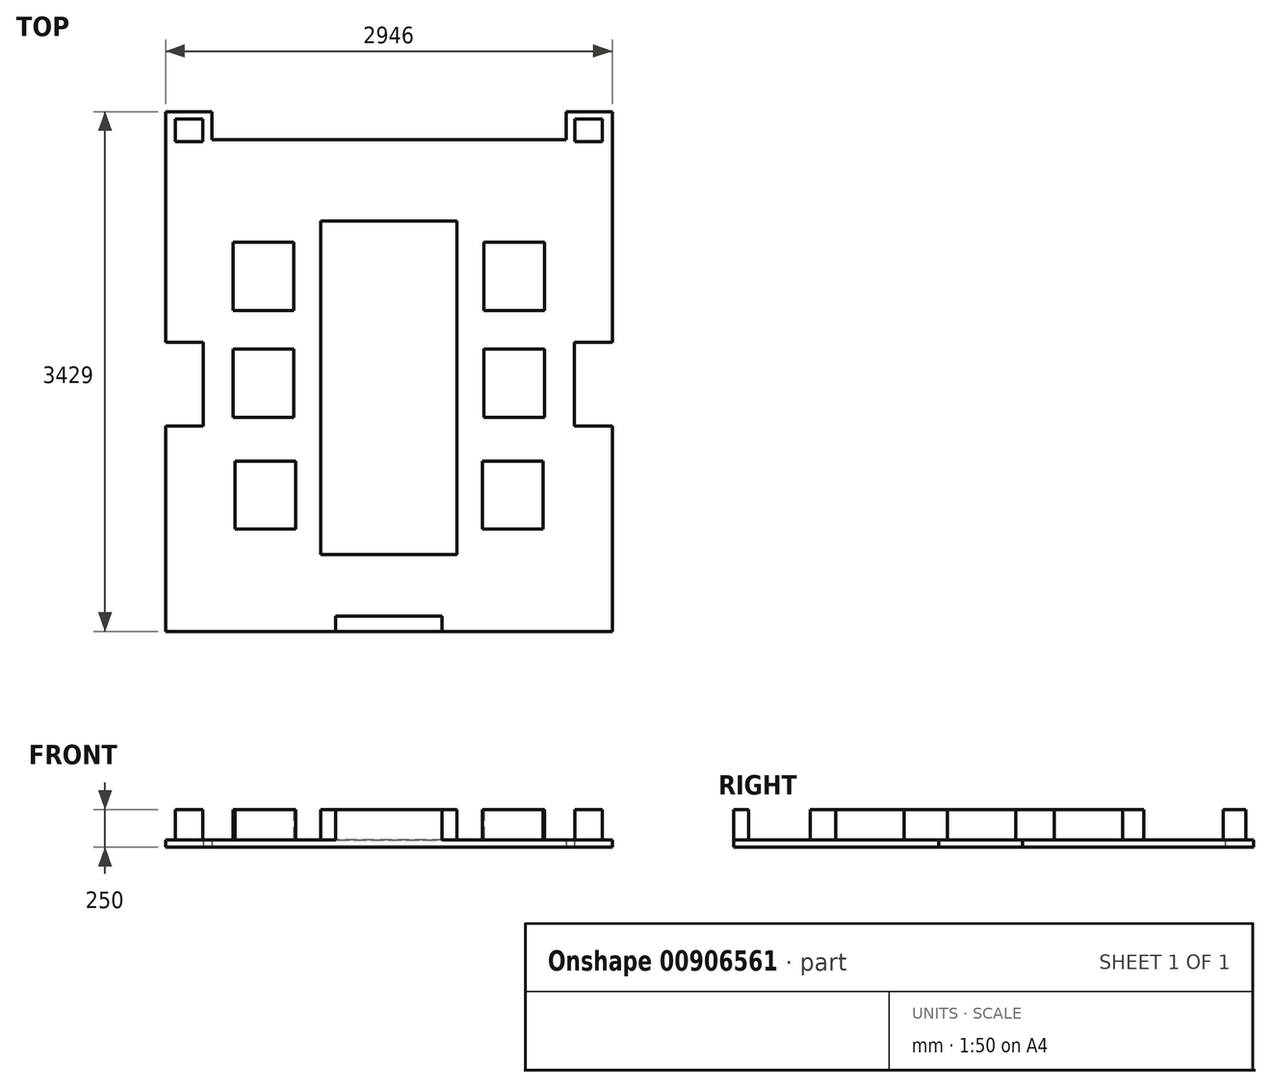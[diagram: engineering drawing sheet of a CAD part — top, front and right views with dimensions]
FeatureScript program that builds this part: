
annotation { "Feature Type Name" : "Feature", "Feature Type Description" : "" }
export const myFeature = defineFeature(function(context is Context, id is Id, definition is map)
    precondition{}
    {
        {
            var Q0;
            Q0=qCreatedBy(makeId("Top.planeOp"),FACE);
            var sketch = newSketch(context, id + "F0", { "sketchPlane" : qUnion([Q0])});
            skLineSegment(sketch, "E0", {"start": v(-1619.5, 3350.46) * mm, "end": v(-1924.5, 3350.46) * mm});
            skLineSegment(sketch, "E1", {"start": v(-1924.5, 3350.46) * mm, "end": v(-1924.5, 1827.07) * mm});
            skLineSegment(sketch, "E2", {"start": v(-1924.5, 1827.07) * mm, "end": v(-1674.5, 1827.07) * mm});
            skLineSegment(sketch, "E3", {"start": v(-1674.5, 1827.07) * mm, "end": v(-1674.5, 1277.07) * mm});
            skLineSegment(sketch, "E4", {"start": v(-1674.5, 1277.07) * mm, "end": v(-1924.5, 1277.07) * mm});
            skLineSegment(sketch, "E5", {"start": v(-1924.5, 1277.07) * mm, "end": v(-1924.5, -78.54) * mm});
            skLineSegment(sketch, "E6", {"start": v(-1924.5, -78.54) * mm, "end": v(1021.5, -78.54) * mm});
            skLineSegment(sketch, "E7", {"start": v(1021.5, -78.54) * mm, "end": v(1021.5, 1277.07) * mm});
            skLineSegment(sketch, "E8", {"start": v(1021.5, 1277.07) * mm, "end": v(771.5, 1277.07) * mm});
            skLineSegment(sketch, "E9", {"start": v(771.5, 1277.07) * mm, "end": v(771.5, 1827.07) * mm});
            skLineSegment(sketch, "E10", {"start": v(771.5, 1827.07) * mm, "end": v(1021.5, 1827.07) * mm});
            skLineSegment(sketch, "E11", {"start": v(1021.5, 1827.07) * mm, "end": v(1021.5, 3350.46) * mm});
            skLineSegment(sketch, "E12", {"start": v(1021.5, 3350.46) * mm, "end": v(716.5, 3350.46) * mm});
            skLineSegment(sketch, "E13", {"start": v(716.5, 3350.46) * mm, "end": v(716.5, 3165.53) * mm});
            skLineSegment(sketch, "E14", {"start": v(716.5, 3165.53) * mm, "end": v(-1619.5, 3165.53) * mm});
            skLineSegment(sketch, "E15", {"start": v(-1619.5, 3165.53) * mm, "end": v(-1619.5, 3350.46) * mm});
            skSolve(sketch);
        }
        {
            var Q0;
            Q0 = qSketchRegion(id + "F0", true);
            extrude(context, id + "F1", {"entities" : qUnion([Q0]), "depth" : 50 * mm, "offsetDistance" : 25 * mm});
        }
        {
            var Q0;
            Q0=makeQuery(id+"F1.opExtrude","CAP_FACE",FACE,{"disambiguationData":[OSD([sQuery(id+"F0.wireOp",EDGE,"E0"),sQuery(id+"F0.wireOp",EDGE,"E1"),sQuery(id+"F0.wireOp",EDGE,"E2"),sQuery(id+"F0.wireOp",EDGE,"E3"),sQuery(id+"F0.wireOp",EDGE,"E4"),sQuery(id+"F0.wireOp",EDGE,"E5"),sQuery(id+"F0.wireOp",EDGE,"E6"),sQuery(id+"F0.wireOp",EDGE,"E7"),sQuery(id+"F0.wireOp",EDGE,"E8"),sQuery(id+"F0.wireOp",EDGE,"E9"),sQuery(id+"F0.wireOp",EDGE,"E10"),sQuery(id+"F0.wireOp",EDGE,"E11"),sQuery(id+"F0.wireOp",EDGE,"E12"),sQuery(id+"F0.wireOp",EDGE,"E13"),sQuery(id+"F0.wireOp",EDGE,"E14"),sQuery(id+"F0.wireOp",EDGE,"E15")])],"isStart":false});
            var sketch = newSketch(context, id + "F2", { "sketchPlane" : qUnion([Q0])});
            skLineSegment(sketch, "E16.bottom", {"start": v(-901.5, 2626.75) * mm, "end": v(-1.5, 2626.75) * mm});
            skLineSegment(sketch, "E16.top", {"start": v(-901.5, 426.75) * mm, "end": v(-1.5, 426.75) * mm});
            skLineSegment(sketch, "E16.left", {"start": v(-901.5, 2626.75) * mm, "end": v(-901.5, 426.75) * mm});
            skLineSegment(sketch, "E16.right", {"start": v(-1.5, 2626.75) * mm, "end": v(-1.5, 426.75) * mm});
            skLineSegment(sketch, "E17.bottom", {"start": v(-1478.61, 2487.53) * mm, "end": v(-1078.61, 2487.53) * mm});
            skLineSegment(sketch, "E17.top", {"start": v(-1478.61, 2037.53) * mm, "end": v(-1078.61, 2037.53) * mm});
            skLineSegment(sketch, "E17.left", {"start": v(-1478.61, 2487.53) * mm, "end": v(-1478.61, 2037.53) * mm});
            skLineSegment(sketch, "E17.right", {"start": v(-1078.61, 2487.53) * mm, "end": v(-1078.61, 2037.53) * mm});
            skLineSegment(sketch, "E18.bottom", {"start": v(-1467.67, 1045.34) * mm, "end": v(-1067.67, 1045.34) * mm});
            skLineSegment(sketch, "E18.top", {"start": v(-1467.67, 595.34) * mm, "end": v(-1067.67, 595.34) * mm});
            skLineSegment(sketch, "E18.left", {"start": v(-1467.67, 1045.34) * mm, "end": v(-1467.67, 595.34) * mm});
            skLineSegment(sketch, "E18.right", {"start": v(-1067.67, 1045.34) * mm, "end": v(-1067.67, 595.34) * mm});
            skLineSegment(sketch, "E19.bottom", {"start": v(-1478.61, 1783.14) * mm, "end": v(-1078.61, 1783.14) * mm});
            skLineSegment(sketch, "E19.top", {"start": v(-1478.61, 1333.14) * mm, "end": v(-1078.61, 1333.14) * mm});
            skLineSegment(sketch, "E19.left", {"start": v(-1478.61, 1783.14) * mm, "end": v(-1478.61, 1333.14) * mm});
            skLineSegment(sketch, "E19.right", {"start": v(-1078.61, 1783.14) * mm, "end": v(-1078.61, 1333.14) * mm});
            skLineSegment(sketch, "E20", {"start": v(-451.5, 2626.75) * mm, "end": v(-451.5, 426.75) * mm});
            skLineSegment(sketch, "E21.MirrorCS", {"start": v(575.6, 2487.53) * mm, "end": v(175.6, 2487.53) * mm});
            skLineSegment(sketch, "E22.MirrorCS", {"start": v(175.6, 2487.53) * mm, "end": v(175.6, 2037.53) * mm});
            skLineSegment(sketch, "E23.MirrorCS", {"start": v(575.6, 2487.53) * mm, "end": v(575.6, 2037.53) * mm});
            skLineSegment(sketch, "E24.MirrorCS", {"start": v(575.6, 2037.53) * mm, "end": v(175.6, 2037.53) * mm});
            skLineSegment(sketch, "E25.MirrorCS", {"start": v(575.6, 1783.14) * mm, "end": v(175.6, 1783.14) * mm});
            skLineSegment(sketch, "E26.MirrorCS", {"start": v(175.6, 1783.14) * mm, "end": v(175.6, 1333.14) * mm});
            skLineSegment(sketch, "E27.MirrorCS", {"start": v(575.6, 1333.14) * mm, "end": v(175.6, 1333.14) * mm});
            skLineSegment(sketch, "E28.MirrorCS", {"start": v(575.6, 1783.14) * mm, "end": v(575.6, 1333.14) * mm});
            skLineSegment(sketch, "E29.MirrorCS", {"start": v(564.66, 1045.34) * mm, "end": v(164.66, 1045.34) * mm});
            skLineSegment(sketch, "E30.MirrorCS", {"start": v(564.66, 1045.34) * mm, "end": v(564.66, 595.34) * mm});
            skLineSegment(sketch, "E31.MirrorCS", {"start": v(564.66, 595.34) * mm, "end": v(164.66, 595.34) * mm});
            skLineSegment(sketch, "E32.MirrorCS", {"start": v(164.66, 1045.34) * mm, "end": v(164.66, 595.34) * mm});
            skLineSegment(sketch, "E33", {"start": v(-1674.5, 1827.07) * mm, "end": v(-1674.5, 1277.07) * mm});
            skLineSegment(sketch, "E34", {"start": v(771.5, 1827.07) * mm, "end": v(771.5, 1277.07) * mm});
            skLineSegment(sketch, "E35.bottom", {"start": v(-1859.5, 3300.46) * mm, "end": v(-1679.5, 3300.46) * mm});
            skLineSegment(sketch, "E35.top", {"start": v(-1859.5, 3150.46) * mm, "end": v(-1679.5, 3150.46) * mm});
            skLineSegment(sketch, "E35.left", {"start": v(-1859.5, 3300.46) * mm, "end": v(-1859.5, 3150.46) * mm});
            skLineSegment(sketch, "E35.right", {"start": v(-1679.5, 3300.46) * mm, "end": v(-1679.5, 3150.46) * mm});
            skLineSegment(sketch, "E36.bottom", {"start": v(776.5, 3300.46) * mm, "end": v(956.5, 3300.46) * mm});
            skLineSegment(sketch, "E36.top", {"start": v(776.5, 3150.46) * mm, "end": v(956.5, 3150.46) * mm});
            skLineSegment(sketch, "E36.left", {"start": v(776.5, 3300.46) * mm, "end": v(776.5, 3150.46) * mm});
            skLineSegment(sketch, "E36.right", {"start": v(956.5, 3300.46) * mm, "end": v(956.5, 3150.46) * mm});
            skLineSegment(sketch, "E37", {"start": v(-451.5, -78.54) * mm, "end": v(-801.5, -78.54) * mm});
            skLineSegment(sketch, "E38", {"start": v(-801.5, -78.54) * mm, "end": v(-801.5, 21.46) * mm});
            skLineSegment(sketch, "E39", {"start": v(-801.5, 21.46) * mm, "end": v(-101.5, 21.46) * mm});
            skLineSegment(sketch, "E40", {"start": v(-101.5, 21.46) * mm, "end": v(-101.5, -78.54) * mm});
            skLineSegment(sketch, "E41", {"start": v(-101.5, -78.54) * mm, "end": v(-451.5, -78.54) * mm});
            skSolve(sketch);
        }
        {
            var Q0;
            Q0 = qSketchRegion(id + "F2", true);
            extrude(context, id + "F3", {"entities" : qUnion([Q0]), "operationType" : NewBodyOperationType.ADD, "depth" : 200 * mm, "offsetDistance" : 25 * mm});
        }
    });
